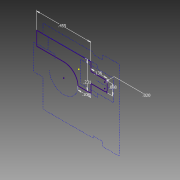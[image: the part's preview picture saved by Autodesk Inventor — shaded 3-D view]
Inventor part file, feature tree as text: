
AUTODESK INVENTOR PART (.ipt)
format: ipt  version: 2014 SP1 (Build 180222100, 222)  size: 138,752 bytes
history: native  units: in
note: dims shown in document units (in); Inventor stores cm internally (conversion verified against a paired STEP export)
features: extrude x3, sketch x3, projected_geometry x2, fillet x1, chamfer x1
ambient origin geometry x8: Origin, YZ Plane, XZ Plane, XY Plane, X Axis, Y Axis, Z Axis, Center Point
bodies: Solid1 (feature_tree)
feature tree (10):
  extrude  "Extrusion1"  Depth=0.2305in
  extrude  "Extrusion2"  Depth=0.0875in
  fillet  "Fillet1"  Radius=0.136in
  extrude  "Extrusion3"  Depth=0.4545in
  chamfer  "Chamfer1"  Distance=0.042in
  sketch  "Sketch1"  dims[d0=0.2305in d1=0.2305in]
  sketch  "Sketch2"  dims[d2=0.4545in d3=0.108in d4=0.0875in d5=0.136in]
  projected_geometry  "Projected Loop1"
  sketch  "Sketch3"  dims[d6=0.02in d7=0.4545in d8=0.042in d9=0.0in d10=0.042in d11=0.122in d12=0.0in d13=0.0781in d14=0.122in d15=0.0in d16=0.01in d17=0.125in d18=45.0deg]
  projected_geometry  "Projected Loop2"
